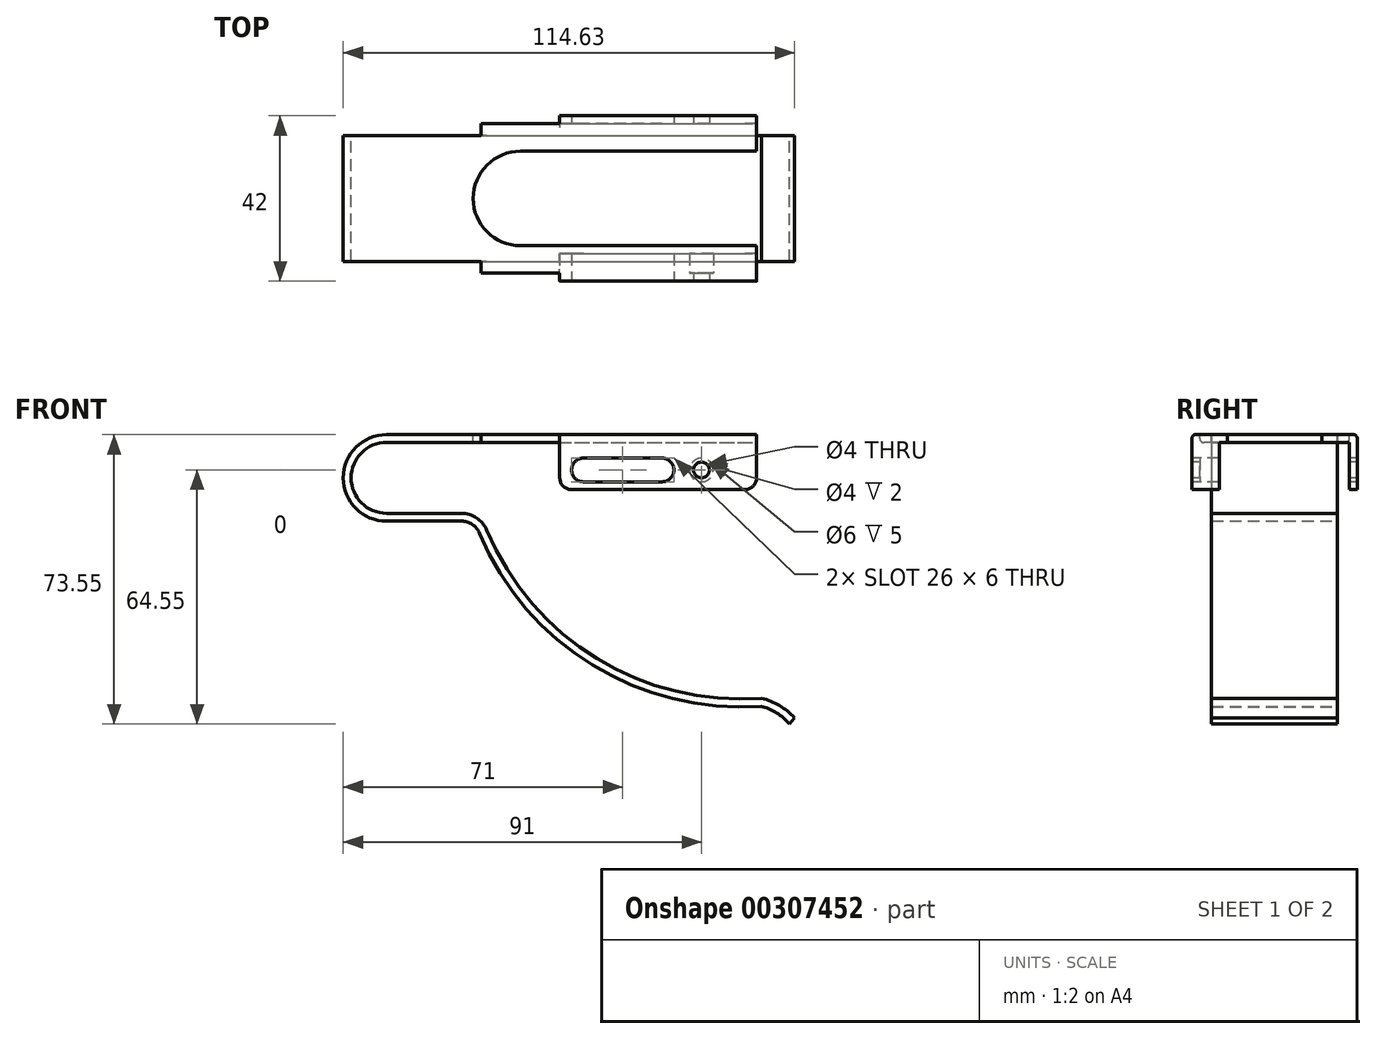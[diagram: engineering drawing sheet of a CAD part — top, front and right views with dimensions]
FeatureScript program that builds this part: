
annotation { "Feature Type Name" : "Feature", "Feature Type Description" : "" }
export const myFeature = defineFeature(function(context is Context, id is Id, definition is map)
    precondition{}
    {
        {
            var Q0;
            Q0=qCreatedBy(makeId("Front.planeOp"),FACE);
            var sketch = newSketch(context, id + "F0", { "sketchPlane" : qUnion([Q0])});
            skArc(sketch, "E0", {"start": v(0, 9) * mm, "mid": v(-9, 0) * mm, "end": v(0, -9) * mm});
            skLineSegment(sketch, "E1", {"start": v(0, 9) * mm, "end": v(94, 9) * mm});
            skLineSegment(sketch, "E2", {"start": v(0, -9) * mm, "end": v(19, -9) * mm});
            skLineSegment(sketch, "E3.0", {"start": v(0, 11) * mm, "end": v(94, 11) * mm});
            skArc(sketch, "E3.2", {"start": v(23.61, -14.06) * mm, "mid": v(52.3, -47.54) * mm, "end": v(95.13, -58.02) * mm});
            skLineSegment(sketch, "E3.3", {"start": v(0, -11) * mm, "end": v(19, -11) * mm});
            skArc(sketch, "E3.4", {"start": v(0, 11) * mm, "mid": v(-11, 0) * mm, "end": v(0, -11) * mm});
            skLineSegment(sketch, "E4", {"start": v(94, 11) * mm, "end": v(94, 9) * mm});
            skPoint(sketch, "E5.visualSharp", {"position": v(22.4, -11) * mm});
            skArc(sketch, "E5.filletArc", {"start": v(23.61, -14.06) * mm, "mid": v(21.77, -11.84) * mm, "end": v(19, -11) * mm});
            skArc(sketch, "E6.0", {"start": v(25.45, -13.3) * mm, "mid": v(22.88, -10.17) * mm, "end": v(19, -9) * mm});
            skArc(sketch, "E7.0", {"start": v(103.63, -61) * mm, "mid": v(99.85, -57.85) * mm, "end": v(95.3, -56) * mm});
            skArc(sketch, "E7.1", {"start": v(25.45, -13.3) * mm, "mid": v(53.48, -45.92) * mm, "end": v(95.3, -56) * mm});
            skLineSegment(sketch, "E8", {"start": v(108.9, -60.95) * mm, "end": v(113.87, -60.95) * mm});
            skArc(sketch, "E9.0", {"start": v(102.33, -62.55) * mm, "mid": v(99.08, -59.72) * mm, "end": v(95.13, -58.02) * mm});
            skLineSegment(sketch, "E10", {"start": v(103.63, -61) * mm, "end": v(102.33, -62.55) * mm});
            skSolve(sketch);
        }
        {
            var Q0;
            Q0 = qSketchRegion(id + "F0", true);
            extrude(context, id + "F1", {"entities" : qUnion([Q0]), "depth" : 16 * mm});
        }
        {
            var Q0;
            Q0=makeQuery(id+"F1.opExtrude","SWEPT_FACE",FACE,{"disambiguationData":[OSD([sQuery(id+"F0.wireOp",EDGE,"E3.0")])]});
            var sketch = newSketch(context, id + "F2", { "sketchPlane" : qUnion([Q0])});
            skLineSegment(sketch, "E11.bottom", {"start": v(24, -16) * mm, "end": v(94, -16) * mm});
            skLineSegment(sketch, "E11.top", {"start": v(24, -19) * mm, "end": v(94, -19) * mm});
            skLineSegment(sketch, "E11.left", {"start": v(24, -16) * mm, "end": v(24, -19) * mm});
            skLineSegment(sketch, "E11.right", {"start": v(94, -16) * mm, "end": v(94, -19) * mm});
            skSolve(sketch);
        }
        {
            var Q0;
            Q0 = qSketchRegion(id + "F2", true);
            extrude(context, id + "F3", {"entities" : qUnion([Q0]), "operationType" : NewBodyOperationType.ADD, "oppositeDirection" : true, "depth" : 2 * mm});
        }
        {
            var Q0;
            Q0=makeQuery(id+"F3.opExtrude","SWEPT_FACE",FACE,{"disambiguationData":[OSD([sQuery(id+"F2.wireOp",EDGE,"E11.top")])]});
            var sketch = newSketch(context, id + "F4", { "sketchPlane" : qUnion([Q0])});
            skLineSegment(sketch, "E12.bottom", {"start": v(44, 11) * mm, "end": v(94, 11) * mm});
            skLineSegment(sketch, "E12.top", {"start": v(44, -3) * mm, "end": v(94, -3) * mm});
            skLineSegment(sketch, "E12.left", {"start": v(44, 11) * mm, "end": v(44, -3) * mm});
            skLineSegment(sketch, "E12.right", {"start": v(94, 11) * mm, "end": v(94, -3) * mm});
            skSolve(sketch);
        }
        {
            var Q0;
            Q0 = qSketchRegion(id + "F4", true);
            extrude(context, id + "F5", {"entities" : qUnion([Q0]), "operationType" : NewBodyOperationType.ADD, "depth" : 2 * mm});
        }
        {
            var Q0;
            Q0=makeQuery(id+"F5.opExtrude","CAP_EDGE",EDGE,{"disambiguationData":[OSD([sQuery(id+"F4.wireOp",EDGE,"E12.bottom")])],"isStart":false});
            var Q1;
            {var subQ0=sQuery(id+"F2.wireOp",EDGE,"E11.top");Q1=makeQuery(id+"F5.boolean.opBoolean","SPLIT",EDGE,{"disambiguationData":[topologyDisambiguationEdgeConnected([makeQuery(id+"F5.opExtrude","CAP_FACE",FACE,{"disambiguationData":[OSD([sQuery(id+"F4.wireOp",EDGE,"E12.bottom"),sQuery(id+"F4.wireOp",EDGE,"E12.top"),sQuery(id+"F4.wireOp",EDGE,"E12.left"),sQuery(id+"F4.wireOp",EDGE,"E12.right")])],"isStart":true})])],"derivedFrom":makeQuery(id+"F3.opExtrude","CAP_EDGE",EDGE,{"disambiguationData":[OSD([subQ0])],"isStart":false})});}
            fillet(context, id + "F6", {"entities" : qUnion([Q0, Q1]), "radius" : 1 * mm, "tangentPropagation" : true, "allowEdgeOverflow" : false});
        }
        {
            var Q0;
            Q0=makeQuery(id+"F1.opExtrude","SWEPT_BODY",BODY,{"disambiguationData":[OSD([sQuery(id+"F0.wireOp",EDGE,"E0"),sQuery(id+"F0.wireOp",EDGE,"E1"),sQuery(id+"F0.wireOp",EDGE,"E2"),sQuery(id+"F0.wireOp",EDGE,"E3.0"),sQuery(id+"F0.wireOp",EDGE,"E3.2"),sQuery(id+"F0.wireOp",EDGE,"E3.3"),sQuery(id+"F0.wireOp",EDGE,"E3.4"),sQuery(id+"F0.wireOp",EDGE,"E4"),sQuery(id+"F0.wireOp",EDGE,"E5.filletArc"),sQuery(id+"F0.wireOp",EDGE,"E6.0"),sQuery(id+"F0.wireOp",EDGE,"E7.0"),sQuery(id+"F0.wireOp",EDGE,"E7.1"),sQuery(id+"F0.wireOp",EDGE,"E9.0"),sQuery(id+"F0.wireOp",EDGE,"E10")])]});
            var Q1;
            Q1=qCreatedBy(makeId("Front.planeOp"),FACE);
            mirror(context, id + "F7", {"operationType" : NewBodyOperationType.ADD, "entities" : qUnion([Q0]), "mirrorPlane" : qUnion([Q1])});
        }
        {
            var Q0;
            {var subQ0=makeQuery(id+"F5.boolean.opBoolean","MERGE",FACE,{"derivedFrom":[makeQuery(id+"F3.boolean.opBoolean","MERGE",FACE,{"derivedFrom":[makeQuery(id+"F1.opExtrude","SWEPT_FACE",FACE,{"disambiguationData":[OSD([sQuery(id+"F0.wireOp",EDGE,"E3.0")])]}),makeQuery(id+"F3.opExtrude","CAP_FACE",FACE,{"disambiguationData":[OSD([sQuery(id+"F2.wireOp",EDGE,"E11.bottom"),sQuery(id+"F2.wireOp",EDGE,"E11.top"),sQuery(id+"F2.wireOp",EDGE,"E11.left"),sQuery(id+"F2.wireOp",EDGE,"E11.right")])],"isStart":true})]}),makeQuery(id+"F5.opExtrude","SWEPT_FACE",FACE,{"disambiguationData":[OSD([sQuery(id+"F4.wireOp",EDGE,"E12.bottom")])]})]});Q0=makeQuery(id+"F7.boolean.opBoolean","MERGE",FACE,{"derivedFrom":[subQ0,makeQuery(id+"F7.opPattern","COPY",FACE,{"derivedFrom":subQ0,"instanceName":"1"})]});}
            var sketch = newSketch(context, id + "F8", { "sketchPlane" : qUnion([Q0])});
            skArc(sketch, "E13", {"start": v(34, 12) * mm, "mid": v(22, 0) * mm, "end": v(34, -12) * mm});
            skLineSegment(sketch, "E14", {"start": v(34, -12) * mm, "end": v(94, -12) * mm});
            skLineSegment(sketch, "E15", {"start": v(34, 12) * mm, "end": v(94, 12) * mm});
            skLineSegment(sketch, "E16", {"start": v(94, 12) * mm, "end": v(94, -12) * mm});
            skSolve(sketch);
        }
        {
            var Q0;
            Q0 = qSketchRegion(id + "F8", true);
            extrude(context, id + "F9", {"entities" : qUnion([Q0]), "operationType" : NewBodyOperationType.REMOVE, "oppositeDirection" : true, "depth" : 2 * mm, "offsetDistance" : 25 * mm});
        }
        {
            var Q0;
            Q0=qCreatedBy(makeId("Front.planeOp"),FACE);
            var sketch = newSketch(context, id + "F10", { "sketchPlane" : qUnion([Q0])});
            skLineSegment(sketch, "E17", {"start": v(50, 2) * mm, "end": v(70, 2) * mm});
            skArc(sketch, "E18.0.startCap", {"start": v(50, -1) * mm, "mid": v(47, 2) * mm, "end": v(50, 5) * mm});
            skArc(sketch, "E18.0.endCap", {"start": v(70, 5) * mm, "mid": v(73, 2) * mm, "end": v(70, -1) * mm});
            skLineSegment(sketch, "E18.0.left", {"start": v(50, 5) * mm, "end": v(70, 5) * mm});
            skLineSegment(sketch, "E18.0.right", {"start": v(50, -1) * mm, "end": v(70, -1) * mm});
            skSolve(sketch);
        }
        {
            var Q0;
            Q0 = qSketchRegion(id + "F10", true);
            extrude(context, id + "F11", {"entities" : qUnion([Q0]), "operationType" : NewBodyOperationType.REMOVE, "endBound" : BoundingType.THROUGH_ALL, "oppositeDirection" : true, "depth" : 25 * mm, "hasSecondDirection" : true, "secondDirectionOppositeDirection" : false, "secondDirectionDepth" : 25 * mm});
        }
        {
            var Q0;
            Q0=makeQuery(id+"F5.opExtrude","CAP_FACE",FACE,{"disambiguationData":[OSD([sQuery(id+"F4.wireOp",EDGE,"E12.bottom"),sQuery(id+"F4.wireOp",EDGE,"E12.top"),sQuery(id+"F4.wireOp",EDGE,"E12.left"),sQuery(id+"F4.wireOp",EDGE,"E12.right")])],"isStart":false});
            var sketch = newSketch(context, id + "F12", { "sketchPlane" : qUnion([Q0])});
            skPoint(sketch, "E19", {"position": v(80, 2) * mm});
            skSolve(sketch);
        }
        {
            var Q0;
            Q0=sQuery(id+"F12.wireOp",VERTEX,"E19");
            var Q1;
            Q1=makeQuery(id+"F1.opExtrude","SWEPT_BODY",BODY,{"disambiguationData":[OSD([sQuery(id+"F0.wireOp",EDGE,"E0"),sQuery(id+"F0.wireOp",EDGE,"E1"),sQuery(id+"F0.wireOp",EDGE,"E2"),sQuery(id+"F0.wireOp",EDGE,"E3.0"),sQuery(id+"F0.wireOp",EDGE,"E3.2"),sQuery(id+"F0.wireOp",EDGE,"E3.3"),sQuery(id+"F0.wireOp",EDGE,"E3.4"),sQuery(id+"F0.wireOp",EDGE,"E4"),sQuery(id+"F0.wireOp",EDGE,"E5.filletArc"),sQuery(id+"F0.wireOp",EDGE,"E6.0"),sQuery(id+"F0.wireOp",EDGE,"E7.0"),sQuery(id+"F0.wireOp",EDGE,"E7.1"),sQuery(id+"F0.wireOp",EDGE,"E9.0"),sQuery(id+"F0.wireOp",EDGE,"E10")])]});
            hole(context, id + "F13", {"style" : HoleStyle.SIMPLE, "endStyle" : HoleEndStyle.THROUGH, "holeDiameter" : 4 * mm, "isTappedThrough" : true, "tappedDepth" : 12 * mm, "tapClearance" : 3, "locations" : qUnion([Q0]), "scope" : qUnion([Q1])});
        }
        {
            var Q0;
            Q0=makeQuery(id+"F5.opExtrude","CAP_FACE",FACE,{"disambiguationData":[OSD([sQuery(id+"F4.wireOp",EDGE,"E12.bottom"),sQuery(id+"F4.wireOp",EDGE,"E12.top"),sQuery(id+"F4.wireOp",EDGE,"E12.left"),sQuery(id+"F4.wireOp",EDGE,"E12.right")])],"isStart":true});
            var sketch = newSketch(context, id + "F14", { "sketchPlane" : qUnion([Q0])});
            skCircle(sketch, "E20.0", {"center": v(-80, 2) * mm, "radius": 2 * mm});
            skCircle(sketch, "E21.0", {"center": v(-80, 2) * mm, "radius": 3 * mm});
            skSolve(sketch);
        }
        {
            var Q0;
            Q0=makeQuery(id+"F14.imprint","IMPRINT",FACE,{"disambiguationData":[TD([[makeQuery(id+"F14.imprint","IMPRINT",EDGE,{"derivedFrom":sQuery(id+"F14.wireOp",EDGE,"E21.0")}),-1.0]])]});
            extrude(context, id + "F15", {"entities" : qUnion([Q0]), "operationType" : NewBodyOperationType.ADD, "depth" : 5 * mm});
        }
        {
            var Q0;
            {var subQ0=sQuery(id+"F4.wireOp",EDGE,"E12.left");var subQ1=sQuery(id+"F4.wireOp",EDGE,"E12.top");Q0=makeQuery(id+"F15.boolean.opBoolean","MERGE",EDGE,{"derivedFrom":[makeQuery(id+"F5.opExtrude","SWEPT_EDGE",EDGE,{"disambiguationData":[OSD([subQ1,subQ0])]}),makeQuery(id+"F15.opExtrude","SWEPT_EDGE",EDGE,{"disambiguationData":[OSD([subQ1,subQ0])]})]});}
            var Q1;
            {var subQ0=sQuery(id+"F4.wireOp",EDGE,"E12.left");var subQ1=sQuery(id+"F4.wireOp",EDGE,"E12.top");Q1=makeQuery(id+"FdBTYDPAWMSssHg_1.1.F15.boolean.opBoolean","MERGE",EDGE,{"derivedFrom":[makeQuery(id+"F7.opPattern","COPY",EDGE,{"derivedFrom":makeQuery(id+"F5.opExtrude","SWEPT_EDGE",EDGE,{"disambiguationData":[OSD([subQ1,subQ0])]}),"instanceName":"1"}),makeQuery(id+"FdBTYDPAWMSssHg_1.1.F15.opExtrude","SWEPT_EDGE",EDGE,{"disambiguationData":[OSD([subQ1,subQ0])]})]});}
            var Q2;
            {var subQ0=sQuery(id+"F4.wireOp",EDGE,"E12.right");var subQ1=sQuery(id+"F4.wireOp",EDGE,"E12.top");Q2=makeQuery(id+"FdBTYDPAWMSssHg_1.1.F15.boolean.opBoolean","MERGE",EDGE,{"derivedFrom":[makeQuery(id+"F7.opPattern","COPY",EDGE,{"derivedFrom":makeQuery(id+"F5.opExtrude","SWEPT_EDGE",EDGE,{"disambiguationData":[OSD([subQ1,subQ0])]}),"instanceName":"1"}),makeQuery(id+"FdBTYDPAWMSssHg_1.1.F15.opExtrude","SWEPT_EDGE",EDGE,{"disambiguationData":[OSD([subQ1,subQ0])]})]});}
            var Q3;
            {var subQ0=sQuery(id+"F4.wireOp",EDGE,"E12.right");var subQ1=sQuery(id+"F4.wireOp",EDGE,"E12.top");Q3=makeQuery(id+"F15.boolean.opBoolean","MERGE",EDGE,{"derivedFrom":[makeQuery(id+"F5.opExtrude","SWEPT_EDGE",EDGE,{"disambiguationData":[OSD([subQ1,subQ0])]}),makeQuery(id+"F15.opExtrude","SWEPT_EDGE",EDGE,{"disambiguationData":[OSD([subQ1,subQ0])]})]});}
            fillet(context, id + "F16", {"entities" : qUnion([Q0, Q1, Q2, Q3]), "radius" : 3 * mm, "tangentPropagation" : true, "allowEdgeOverflow" : false});
        }
    });
